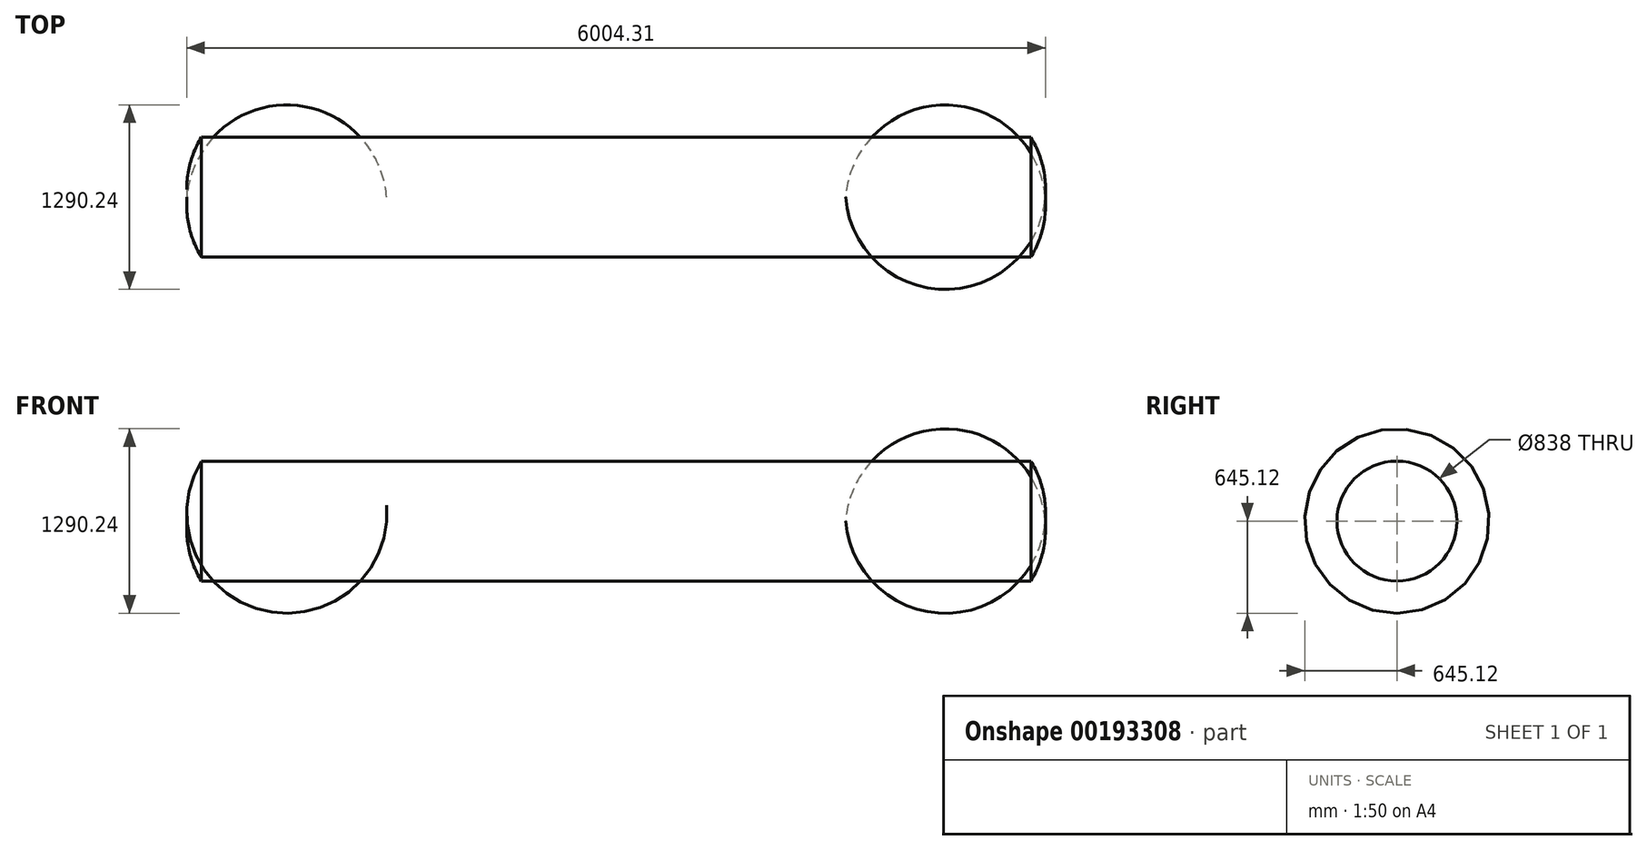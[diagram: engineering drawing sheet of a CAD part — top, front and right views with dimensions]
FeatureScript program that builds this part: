
annotation { "Feature Type Name" : "Feature", "Feature Type Description" : "" }
export const myFeature = defineFeature(function(context is Context, id is Id, definition is map)
    precondition{}
    {
        {
            var Q0;
            Q0=qCreatedBy(makeId("Front.planeOp"),FACE);
            var sketch = newSketch(context, id + "F0", { "sketchPlane" : qUnion([Q0])});
            skLineSegment(sketch, "E0.bottom", {"start": v(-3323.35, 0) * mm, "end": v(2476.65, 0) * mm});
            skLineSegment(sketch, "E0.top", {"start": v(-3323.35, 419) * mm, "end": v(2476.65, 419) * mm});
            skLineSegment(sketch, "E1", {"start": v(-3323.35, 0) * mm, "end": v(-3423.35, 0) * mm});
            skLineSegment(sketch, "E2", {"start": v(2476.65, 0) * mm, "end": v(2576.65, 0) * mm});
            skArc(sketch, "E3", {"start": v(-3323.35, 419) * mm, "mid": v(-3406.38, 217.38) * mm, "end": v(-3423.35, 0) * mm});
            skArc(sketch, "E4", {"start": v(2576.65, 0) * mm, "mid": v(2559.68, 217.38) * mm, "end": v(2476.65, 419) * mm});
            skLineSegment(sketch, "E5", {"start": v(-3323.35, -173.09) * mm, "end": v(-3323.35, 0) * mm, "construction": true});
            skLineSegment(sketch, "E6.trimOffspring", {"start": v(-3323.35, 419) * mm, "end": v(-3323.35, 759.94) * mm, "construction": true});
            skLineSegment(sketch, "E7", {"start": v(-3752.02, 0) * mm, "end": v(2910.95, 0) * mm, "construction": true});
            skSolve(sketch);
        }
        {
            var Q0;
            Q0=makeQuery(id+"F0.imprint","IMPRINT",FACE,{"disambiguationData":[TD([[makeQuery(id+"F0.imprint","IMPRINT",EDGE,{"derivedFrom":sQuery(id+"F0.wireOp",EDGE,"E0.bottom")}),1.0]])]});
            var Q1;
            Q1=sQuery(id+"F0.wireOp",EDGE,"E7");
            revolve(context, id + "F1", {"entities" : qUnion([Q0]), "axis" : qUnion([Q1]), "revolveType" : RevolveType.FULL});
        }
    });
